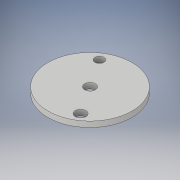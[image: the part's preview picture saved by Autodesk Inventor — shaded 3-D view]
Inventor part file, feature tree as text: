
AUTODESK INVENTOR PART (.ipt)
format: ipt  version: 2019 (Build 230136000, 136)  size: 107,008 bytes
history: native  units: mm
features: extrude x1, sketch x1
ambient origin geometry x8: Origin, YZ Plane, XZ Plane, XY Plane, X Axis, Y Axis, Z Axis, Center Point
bodies: Solid1 (feature_tree)
feature tree (2):
  extrude  "Extrusion1"  Depth=2.0mm
  sketch  "Sketch1"  dims[d0=30.0mm d1=3.8mm d2=3.18mm d3=12.0mm d4=10.0mm d10=12.0mm d11=3.8mm d12=10.0mm d13=2.0mm d14=0.0mm]
